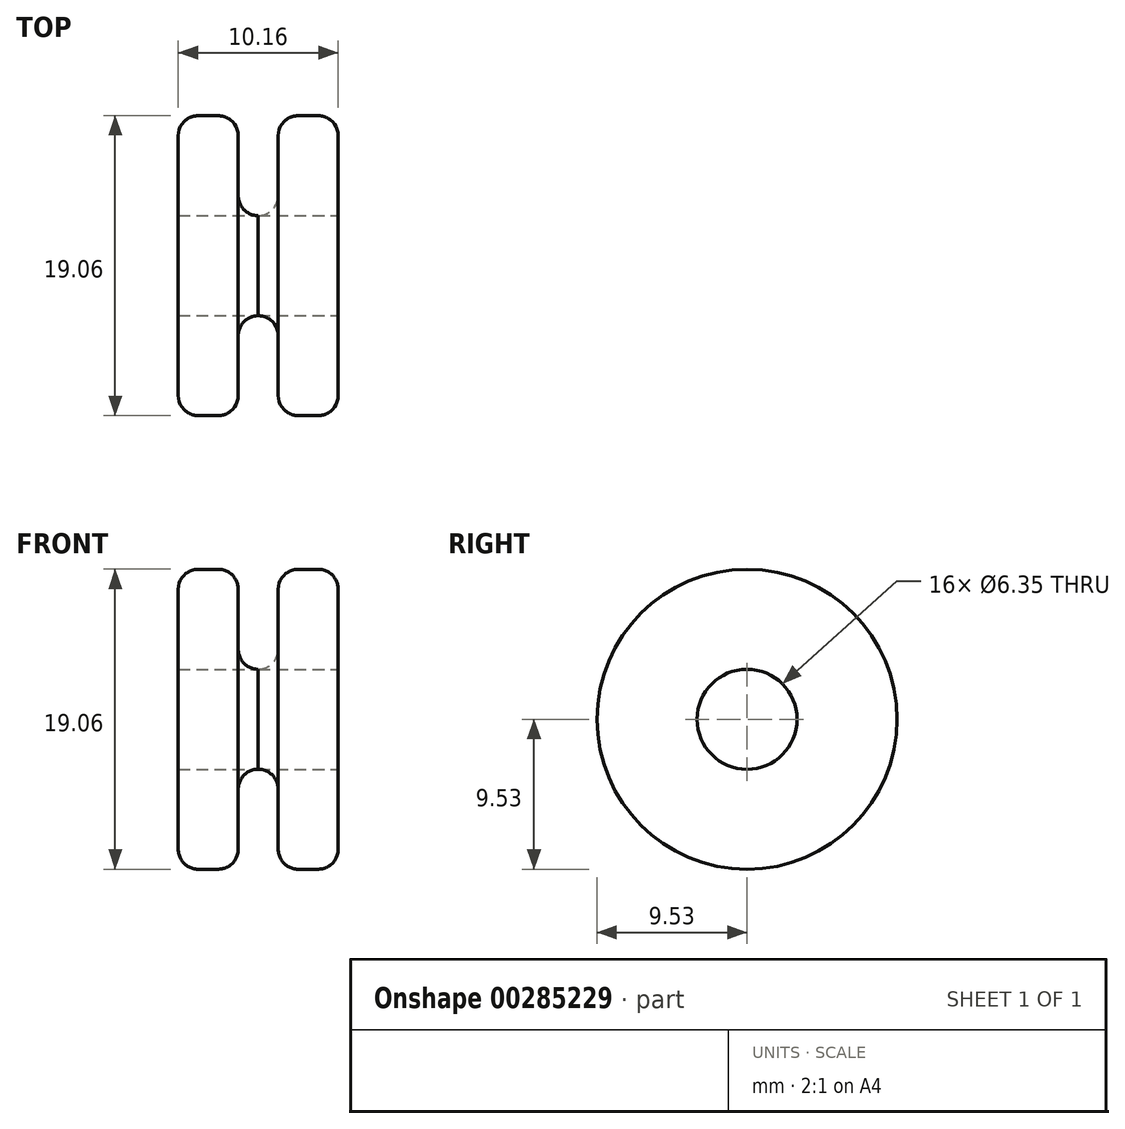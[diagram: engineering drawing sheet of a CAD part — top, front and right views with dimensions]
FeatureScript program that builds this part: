
annotation { "Feature Type Name" : "Feature", "Feature Type Description" : "" }
export const myFeature = defineFeature(function(context is Context, id is Id, definition is map)
    precondition{}
    {
        {
            var Q0;
            Q0=qCreatedBy(makeId("Front.planeOp"),FACE);
            var sketch = newSketch(context, id + "F0", { "sketchPlane" : qUnion([Q0])});
            skLineSegment(sketch, "E0", {"start": v(0, 0) * mm, "end": v(10.16, 0) * mm});
            skLineSegment(sketch, "E1", {"start": v(10.16, 0) * mm, "end": v(10.16, 9.53) * mm});
            skLineSegment(sketch, "E2", {"start": v(10.16, 9.53) * mm, "end": v(6.35, 9.53) * mm});
            skLineSegment(sketch, "E3", {"start": v(6.35, 9.52) * mm, "end": v(6.35, 3.17) * mm});
            skLineSegment(sketch, "E4", {"start": v(6.35, 3.17) * mm, "end": v(3.81, 3.17) * mm});
            skLineSegment(sketch, "E5", {"start": v(3.81, 3.17) * mm, "end": v(3.81, 9.53) * mm});
            skLineSegment(sketch, "E6", {"start": v(3.81, 9.53) * mm, "end": v(0, 9.53) * mm});
            skLineSegment(sketch, "E7", {"start": v(0, 9.53) * mm, "end": v(0, 0) * mm});
            skSolve(sketch);
        }
        {
            var Q0;
            Q0=makeQuery(id+"F0.imprint","IMPRINT",FACE,{"disambiguationData":[TD([[makeQuery(id+"F0.imprint","IMPRINT",EDGE,{"derivedFrom":sQuery(id+"F0.wireOp",EDGE,"E0")}),1.0]])]});
            var Q1;
            Q1=sQuery(id+"F0.wireOp",EDGE,"E0");
            revolve(context, id + "F1", {"entities" : qUnion([Q0]), "axis" : qUnion([Q1]), "revolveType" : RevolveType.FULL});
        }
        {
            var Q0;
            Q0=makeQuery(id+"F1.opRevolve","SWEPT_EDGE",EDGE,{"disambiguationData":[OSD([sQuery(id+"F0.wireOp",EDGE,"E1"),sQuery(id+"F0.wireOp",EDGE,"E2")])]});
            var Q1;
            Q1=makeQuery(id+"F1.opRevolve","SWEPT_EDGE",EDGE,{"disambiguationData":[OSD([sQuery(id+"F0.wireOp",EDGE,"E2"),sQuery(id+"F0.wireOp",EDGE,"E3")])]});
            var Q2;
            Q2=makeQuery(id+"F1.opRevolve","SWEPT_EDGE",EDGE,{"disambiguationData":[OSD([sQuery(id+"F0.wireOp",EDGE,"E5"),sQuery(id+"F0.wireOp",EDGE,"E6")])]});
            var Q3;
            Q3=makeQuery(id+"F1.opRevolve","SWEPT_EDGE",EDGE,{"disambiguationData":[OSD([sQuery(id+"F0.wireOp",EDGE,"E6"),sQuery(id+"F0.wireOp",EDGE,"E7")])]});
            var Q4;
            Q4=makeQuery(id+"F1.opRevolve","SWEPT_EDGE",EDGE,{"disambiguationData":[OSD([sQuery(id+"F0.wireOp",EDGE,"E4"),sQuery(id+"F0.wireOp",EDGE,"E5")])]});
            var Q5;
            Q5=makeQuery(id+"F1.opRevolve","SWEPT_EDGE",EDGE,{"disambiguationData":[OSD([sQuery(id+"F0.wireOp",EDGE,"E3"),sQuery(id+"F0.wireOp",EDGE,"E4")])]});
            fillet(context, id + "F2", {"entities" : qUnion([Q0, Q1, Q2, Q3, Q4, Q5]), "radius" : 1.27 * mm, "tangentPropagation" : true, "allowEdgeOverflow" : false});
        }
        {
            var Q0;
            Q0=makeQuery(id+"F1.opRevolve","SWEPT_FACE",FACE,{"disambiguationData":[OSD([sQuery(id+"F0.wireOp",EDGE,"E1")])]});
            var sketch = newSketch(context, id + "F3", { "sketchPlane" : qUnion([Q0])});
            skCircle(sketch, "E8", {"center": v(0, 0) * mm, "radius": 3.18 * mm});
            skSolve(sketch);
        }
        {
            var Q0;
            Q0=makeQuery(id+"F3.imprint","IMPRINT",FACE,{"disambiguationData":[TD([[makeQuery(id+"F3.imprint","IMPRINT",EDGE,{"derivedFrom":sQuery(id+"F3.wireOp",EDGE,"E8")}),1.0]])]});
            extrude(context, id + "F4", {"entities" : qUnion([Q0]), "operationType" : NewBodyOperationType.REMOVE, "oppositeDirection" : true, "depth" : 25.4 * mm});
        }
    });
